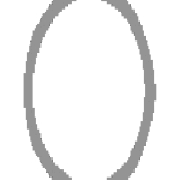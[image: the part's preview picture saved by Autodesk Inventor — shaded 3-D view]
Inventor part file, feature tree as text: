
AUTODESK INVENTOR PART (.ipt)
format: ipt  version: 2021 (Build 250183000, 183)  size: 110,080 bytes
history: native  units: in
note: dims shown in document units (in); Inventor stores cm internally (conversion verified against a paired STEP export)
features: other x4, sketch x3, plane x1
ambient origin geometry x8: Origin, YZ Plane, XZ Plane, XY Plane, X Axis, Y Axis, Z Axis, Center Point
bodies: Solid1 (feature_tree), Body (feature_tree)
feature tree (8):
  other  "Driven Length"
  other  "Frame Generator"
  other  "Start Plane"
  other  "End Plane"
  sketch  "Sketch"  dims[d2=8.3217in d4=-0.0in d5=8.3217in d6=0.12in d7=0.0in d8=90.0deg d9=8.3217in]
  sketch  "Sketch2"  dims[d0=1.0in]
  plane  "Work Plane3"
  sketch  "Sketch3"  dims[d1=0.065in]
